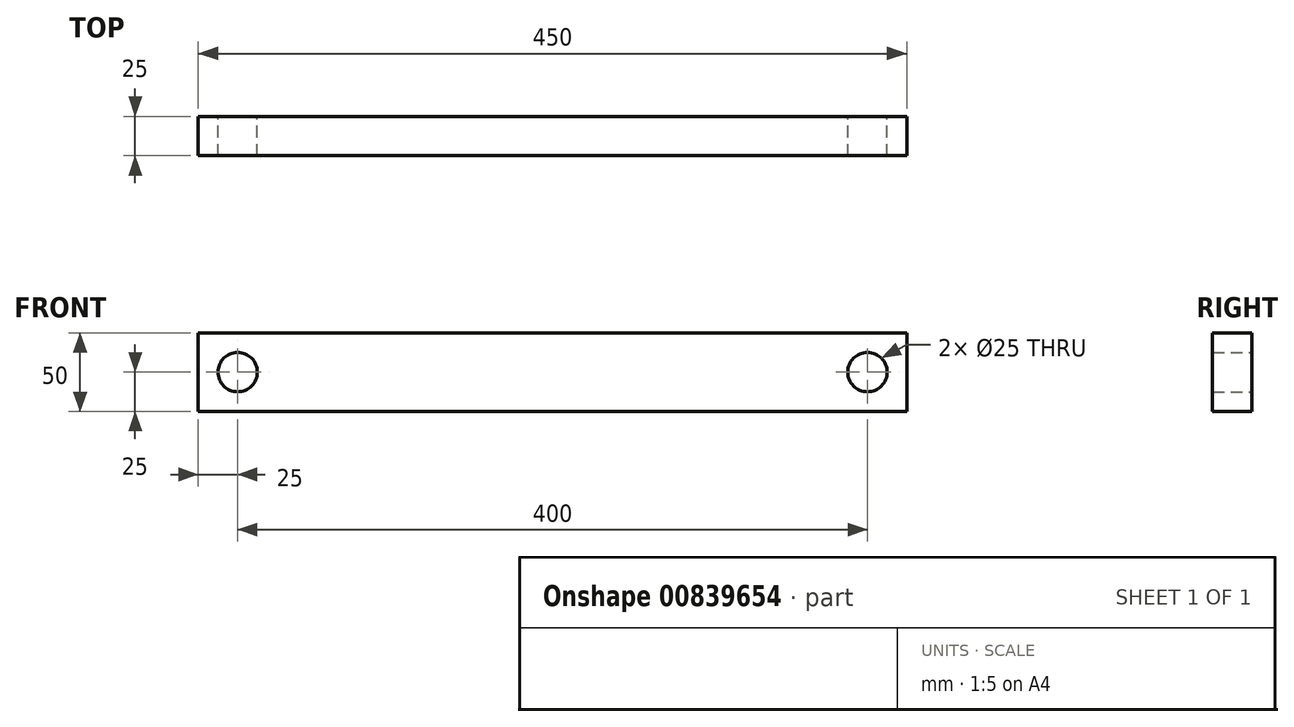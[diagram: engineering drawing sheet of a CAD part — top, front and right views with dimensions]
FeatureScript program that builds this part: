
annotation { "Feature Type Name" : "Feature", "Feature Type Description" : "" }
export const myFeature = defineFeature(function(context is Context, id is Id, definition is map)
    precondition{}
    {
        {
            var Q0;
            Q0=qCreatedBy(makeId("Front.planeOp"),FACE);
            var sketch = newSketch(context, id + "F0", { "sketchPlane" : qUnion([Q0])});
            skCircle(sketch, "E0", {"center": v(-200, 0) * mm, "radius": 12.5 * mm});
            skCircle(sketch, "E1", {"center": v(200, 0) * mm, "radius": 12.5 * mm});
            skLineSegment(sketch, "E2", {"start": v(-200, 0) * mm, "end": v(200, 0) * mm, "construction": true});
            skPoint(sketch, "E3", {"position": v(0, 0) * mm});
            skLineSegment(sketch, "E4.bottom", {"start": v(-225, 25) * mm, "end": v(225, 25) * mm});
            skLineSegment(sketch, "E4.top", {"start": v(-225, -25) * mm, "end": v(225, -25) * mm});
            skLineSegment(sketch, "E4.left", {"start": v(-225, 25) * mm, "end": v(-225, -25) * mm});
            skLineSegment(sketch, "E4.right", {"start": v(225, 25) * mm, "end": v(225, -25) * mm});
            skLineSegment(sketch, "E5", {"start": v(200, 0) * mm, "end": v(225, 25) * mm, "construction": true});
            skLineSegment(sketch, "E6", {"start": v(200, 0) * mm, "end": v(225, -25) * mm, "construction": true});
            skLineSegment(sketch, "E7", {"start": v(-200, 0) * mm, "end": v(-225, 25) * mm, "construction": true});
            skLineSegment(sketch, "E8", {"start": v(-200, 0) * mm, "end": v(-225, -25) * mm, "construction": true});
            skSolve(sketch);
        }
        {
            var Q0;
            Q0=makeQuery(id+"F0.imprint","IMPRINT",FACE,{"disambiguationData":[TD([[makeQuery(id+"F0.imprint","IMPRINT",EDGE,{"derivedFrom":sQuery(id+"F0.wireOp",EDGE,"E0")}),-1.0]])]});
            extrude(context, id + "F1", {"entities" : qUnion([Q0]), "depth" : 25 * mm, "offsetDistance" : 25 * mm});
        }
    });
